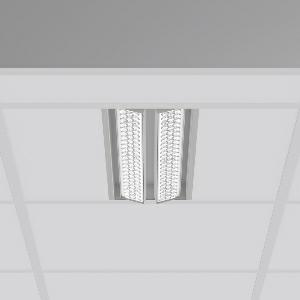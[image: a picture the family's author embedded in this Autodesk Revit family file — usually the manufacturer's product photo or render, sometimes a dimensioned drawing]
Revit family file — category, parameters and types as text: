
# Revit family: tx-move_901734_004_2_06ec
name_source: partatom
category: Lighting Fixtures
units: mm (PartAtom-declared; Revit-internal decimal feet)

## family parameters
Cut with Voids When Loaded = No
Host = Face
Light Source = No
Part Type = Normal
Room Calculation Point = No
Round Connector Dimension = Use Diameter
Shared = No

## types (1)
- MultiLumen 1 (1 x LED Modul 927, 1925 lm, 2700)
    Apparent Load = 32 VA
    Approval mark = CE
    CIE Flux Codes = 65 90 98 100 100
    Color Rendering = 92
    Color Temperature = 2700
    Default Elevation = 1800 mm
    Description = Series: TX-MOVE
Einlege/Einbau-Flächenstrahler. Housing: sheet steel, powder-coated. 2xSwivel range: 90°. High-efficiency LED units with optimum light control thanks to clear plastic (PC) lens optics. Spezielle Mikrostrukturen reduzieren Gelbsaum. Asymmetrical light distribution. Suitable for laying in grid ceiling module 600. Connected converter included in separate gearbox.Suitable for through-wiring.MultiLumen: Luminous flux adjustable in 3 steps. Accessories: Mounting frame for installation in suspended ceilings. Environmentally friendly and resource-saving due to replaceable and recyclable components. 
Colour: silver, matt (approx. RAL 9006)
Length: 597 mm
Width: 190 mm
Height: 39 mm
Cut-out length: 577.5 mm
Cut-out width: 174 mm
Recess height: 100 mm
Lamp: LED
Socket: without socket
Colour temperature: 2700K
Colour rendering index (CRI): 90
System power: 32 W
Rated luminous flux: 3850 lm
Luminous efficiency: 120 lm/W
System power 2: 43 W
Rated luminous flux 2: 4850 lm
Luminous efficiency 2: 113 lm/W
System power 3: 62 W
Rated luminous flux 3: 6450 lm
Luminous efficiency 3: 104 lm/W
Control gear: Regulated power supply
Protection class: I
Type of protection: IP 20
    Height = 0 mm  [stored 0 ft]
    Lamp = 1 x LED Modul 927
    Lamp Light Flux = 1925 lm
    Lamp count = 1
    Length = 597 mm
    Lifetime = 50000 h
    Luminous efficacy = 120 lm/W
    Manufacturer = RZB
    ModVariant = No
    Model = 901734.004.2
    Mounting Place = Ceiling, Wall
    Mounting Type = Recessed
    Number of Poles = 1
    OnlyDefault = Yes
    Power Factor = 1
    Product Name = TX-MOVE
    Product group = Recessed projectors
    ProductGroupID = 401
    Protection Class = Protection class I
    Protection Degree = IP 20
    RLX_Detail_Level = 1
    RLX_Emergency_Light_Flux = 0 lm
    RLX_Emergency_Type = 0
    RLX_Emergency_Type_DB = No
    RlxData = <blob elided: 56533 chars, md5=ba54153f>
    Socket = socket
    Standby Power = 0 W
    System Light Flux = 3850 lm
    System Power = 32 W
    Type Comments = MultiLumen 1
    Type Image = 901733.004.jpg
    URL = http://relux.com
    VarID = multilumen_1
    Voltage = 230 V
    Voltage Range = 220-240 V
    Weight = 0.00 kg
    Width = 190 mm  [stored 0.62336 ft]

note: [stored X ft] marks values corroborated as IEEE doubles in the binary element streams (Revit-internal decimal feet)

## geometry (parser evidence)
native form markers: Blend x4, Sweep x16
no freeform markers — native parametric forms only
